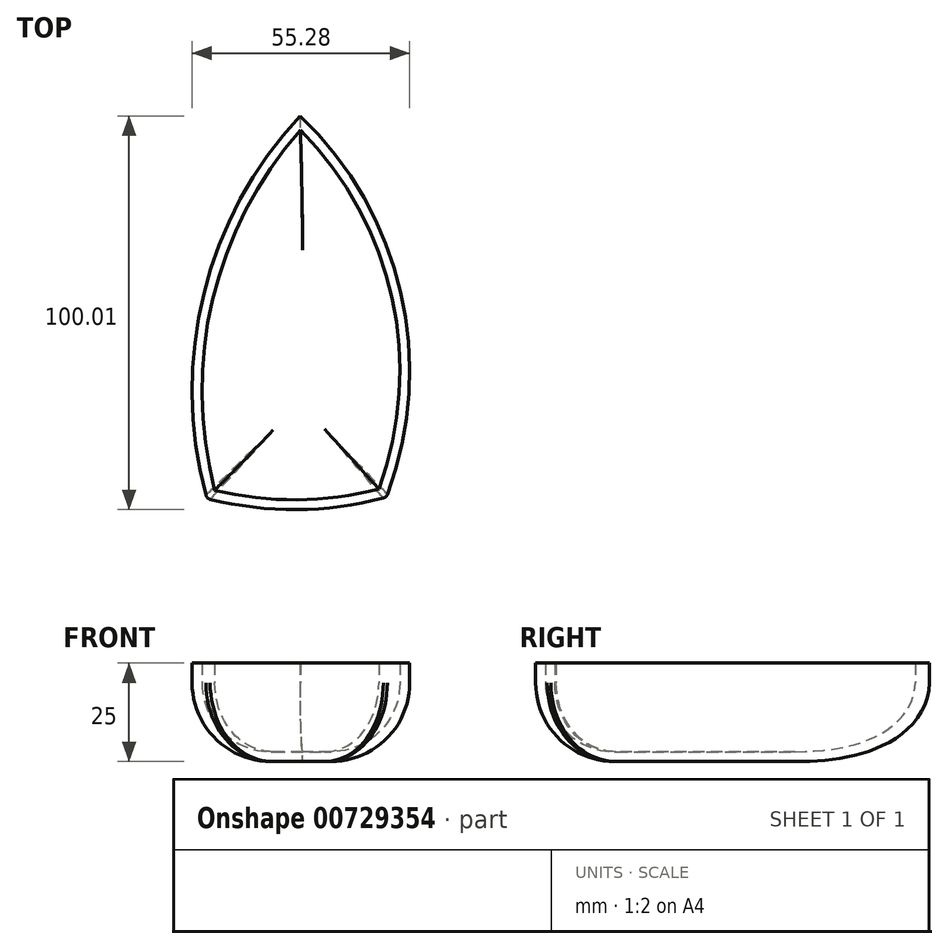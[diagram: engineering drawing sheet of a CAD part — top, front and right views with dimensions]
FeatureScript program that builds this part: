
annotation { "Feature Type Name" : "Feature", "Feature Type Description" : "" }
export const myFeature = defineFeature(function(context is Context, id is Id, definition is map)
    precondition{}
    {
        {
            var Q0;
            Q0=qCreatedBy(makeId("Top.planeOp"),FACE);
            var sketch = newSketch(context, id + "F0", { "sketchPlane" : qUnion([Q0])});
            skArc(sketch, "E0", {"start": v(0, 56.51) * mm, "mid": v(-24.47, 11) * mm, "end": v(-23.65, -40.65) * mm});
            skArc(sketch, "E1", {"start": v(21.95, -40.37) * mm, "mid": v(25.7, 11.4) * mm, "end": v(0, 56.51) * mm});
            skArc(sketch, "E2", {"start": v(-23.65, -40.65) * mm, "mid": v(-0.83, -43.5) * mm, "end": v(21.95, -40.37) * mm});
            skSolve(sketch);
        }
        {
            var Q0;
            Q0=makeQuery(id+"F0.imprint","IMPRINT",FACE,{"disambiguationData":[TD([[makeQuery(id+"F0.imprint","IMPRINT",EDGE,{"derivedFrom":sQuery(id+"F0.wireOp",EDGE,"E0")}),1.0]])]});
            var Q1;
            Q1=sQuery(id+"F0.wireOp",EDGE,"E2");
            var Q2;
            Q2=sQuery(id+"F0.wireOp",EDGE,"E1");
            var Q3;
            Q3=sQuery(id+"F0.wireOp",EDGE,"E0");
            extrude(context, id + "F1", {"entities" : qUnion([Q0]), "surfaceEntities" : qUnion([Q1, Q2, Q3]), "depth" : 25 * mm, "offsetDistance" : 25 * mm});
        }
        {
            var Q0;
            Q0=makeQuery(id+"F1.opExtrude","CAP_FACE",FACE,{"disambiguationData":[OSD([sQuery(id+"F0.wireOp",EDGE,"E0"),sQuery(id+"F0.wireOp",EDGE,"E1"),sQuery(id+"F0.wireOp",EDGE,"E2")])],"isStart":true});
            fillet(context, id + "F2", {"entities" : qUnion([Q0]), "radius" : 20 * mm, "tangentPropagation" : true, "allowEdgeOverflow" : false});
        }
        {
            var Q0;
            Q0=makeQuery(id+"F2.opFillet","BLEND_EDGE",EDGE,{"blendedFrom":[makeQuery(id+"F1.opExtrude","CAP_EDGE",EDGE,{"disambiguationData":[OSD([sQuery(id+"F0.wireOp",EDGE,"E0")])],"isStart":true}),makeQuery(id+"F1.opExtrude","CAP_EDGE",EDGE,{"disambiguationData":[OSD([sQuery(id+"F0.wireOp",EDGE,"E2")])],"isStart":true})],"blendedInto":[]});
            var Q1;
            Q1=makeQuery(id+"F2.opFillet","BLEND_EDGE",EDGE,{"blendedFrom":[makeQuery(id+"F1.opExtrude","CAP_EDGE",EDGE,{"disambiguationData":[OSD([sQuery(id+"F0.wireOp",EDGE,"E1")])],"isStart":true}),makeQuery(id+"F1.opExtrude","CAP_EDGE",EDGE,{"disambiguationData":[OSD([sQuery(id+"F0.wireOp",EDGE,"E2")])],"isStart":true})],"blendedInto":[]});
            fillet(context, id + "F3", {"entities" : qUnion([Q0, Q1]), "radius" : 1.5 * mm, "tangentPropagation" : true, "allowEdgeOverflow" : false});
        }
        {
            var Q0;
            Q0=makeQuery(id+"F1.opExtrude","CAP_FACE",FACE,{"disambiguationData":[OSD([sQuery(id+"F0.wireOp",EDGE,"E0"),sQuery(id+"F0.wireOp",EDGE,"E1"),sQuery(id+"F0.wireOp",EDGE,"E2")])],"isStart":false});
            extrude(context, id + "F4", {"entities" : qUnion([Q0]), "operationType" : NewBodyOperationType.ADD, "depth" : 0 * mm, "offsetDistance" : 25 * mm, "hasSecondDirection" : true, "secondDirectionOppositeDirection" : true, "secondDirectionDepth" : 2 * mm});
        }
        {
            var Q0;
            Q0=makeQuery(id+"F1.opExtrude","CAP_FACE",FACE,{"disambiguationData":[OSD([sQuery(id+"F0.wireOp",EDGE,"E0"),sQuery(id+"F0.wireOp",EDGE,"E1"),sQuery(id+"F0.wireOp",EDGE,"E2")])],"isStart":false});
            shell(context, id + "F5", {"entities" : qUnion([Q0]), "thickness" : 2.5 * mm});
        }
    });
